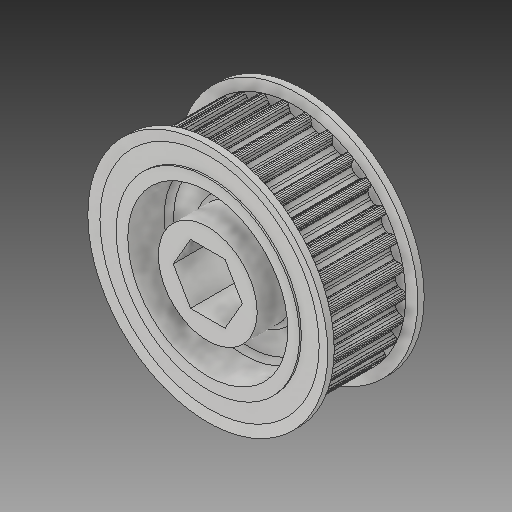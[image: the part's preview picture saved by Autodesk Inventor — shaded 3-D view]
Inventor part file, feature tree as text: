
AUTODESK INVENTOR PART (.ipt)
format: ipt  version: 2017 (Build 210142000, 142)  size: 979,968 bytes
history: native  units: in
note: dims shown in document units (in); Inventor stores cm internally (conversion verified against a paired STEP export)
features: mirror x1
ambient origin geometry x8: Origin, YZ Plane, XZ Plane, XY Plane, X Axis, Y Axis, Z Axis, Center Point
bodies: Solid1 (feature_tree)
feature tree (1):
  mirror  "Mirror1"
